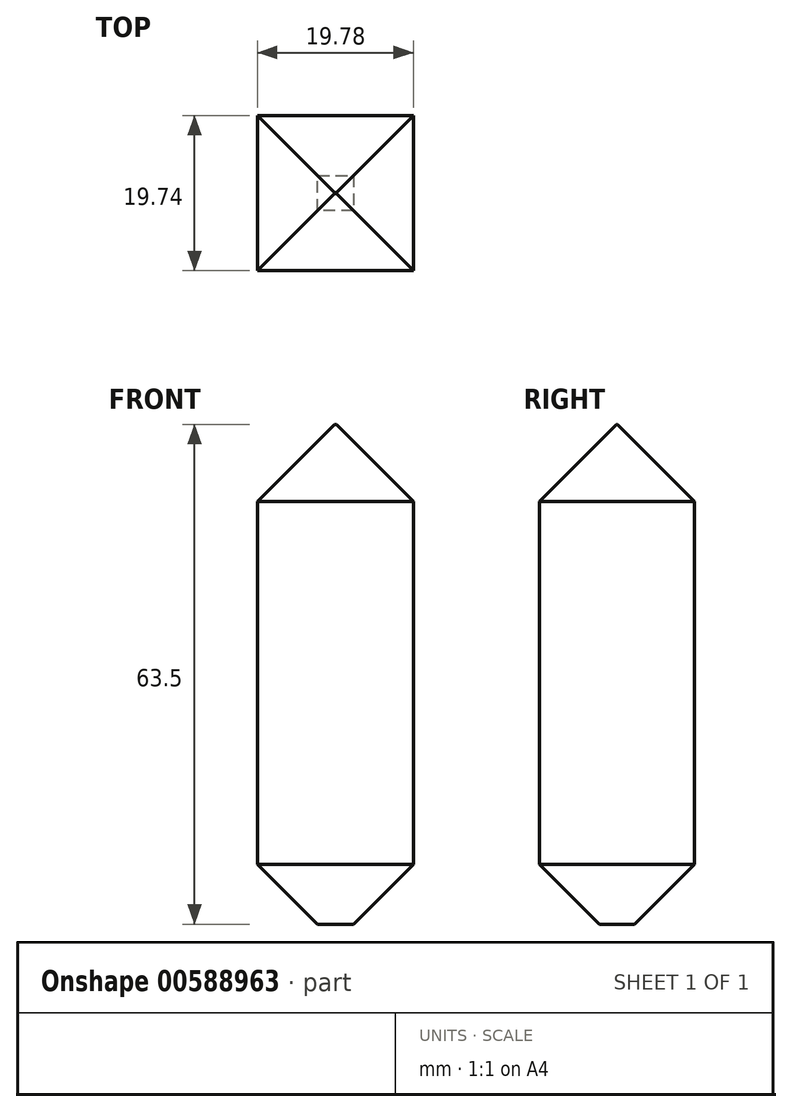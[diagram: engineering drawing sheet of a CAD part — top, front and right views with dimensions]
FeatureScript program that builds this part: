
annotation { "Feature Type Name" : "Feature", "Feature Type Description" : "" }
export const myFeature = defineFeature(function(context is Context, id is Id, definition is map)
    precondition{}
    {
        {
            var Q0;
            Q0=qCreatedBy(makeId("Top.planeOp"),FACE);
            var sketch = newSketch(context, id + "F0", { "sketchPlane" : qUnion([Q0])});
            skLineSegment(sketch, "E0.bottom", {"start": v(0, 0) * mm, "end": v(-19.78, 0) * mm});
            skLineSegment(sketch, "E0.top", {"start": v(0, 19.74) * mm, "end": v(-19.78, 19.74) * mm});
            skLineSegment(sketch, "E0.left", {"start": v(0, 0) * mm, "end": v(0, 19.74) * mm});
            skLineSegment(sketch, "E0.right", {"start": v(-19.78, 0) * mm, "end": v(-19.78, 19.74) * mm});
            skSolve(sketch);
        }
        {
            var Q0;
            Q0 = qSketchRegion(id + "F0", true);
            extrude(context, id + "F1", {"entities" : qUnion([Q0]), "depth" : 63.5 * mm, "offsetDistance" : 25.4 * mm});
        }
        {
            var Q0;
            Q0=makeQuery(id+"F1.opExtrude","CAP_FACE",FACE,{"disambiguationData":[OSD([sQuery(id+"F0.wireOp",EDGE,"E0.bottom"),sQuery(id+"F0.wireOp",EDGE,"E0.top"),sQuery(id+"F0.wireOp",EDGE,"E0.left"),sQuery(id+"F0.wireOp",EDGE,"E0.right")])],"isStart":false});
            chamfer(context, id + "F2", {"entities" : qUnion([Q0]), "width" : 9.78 * mm});
        }
        {
            var Q0;
            Q0=makeQuery(id+"F1.opExtrude","CAP_FACE",FACE,{"disambiguationData":[OSD([sQuery(id+"F0.wireOp",EDGE,"E0.bottom"),sQuery(id+"F0.wireOp",EDGE,"E0.top"),sQuery(id+"F0.wireOp",EDGE,"E0.left"),sQuery(id+"F0.wireOp",EDGE,"E0.right")])],"isStart":true});
            chamfer(context, id + "F3", {"entities" : qUnion([Q0]), "width" : 7.62 * mm, "tangentPropagation" : true});
        }
    });
